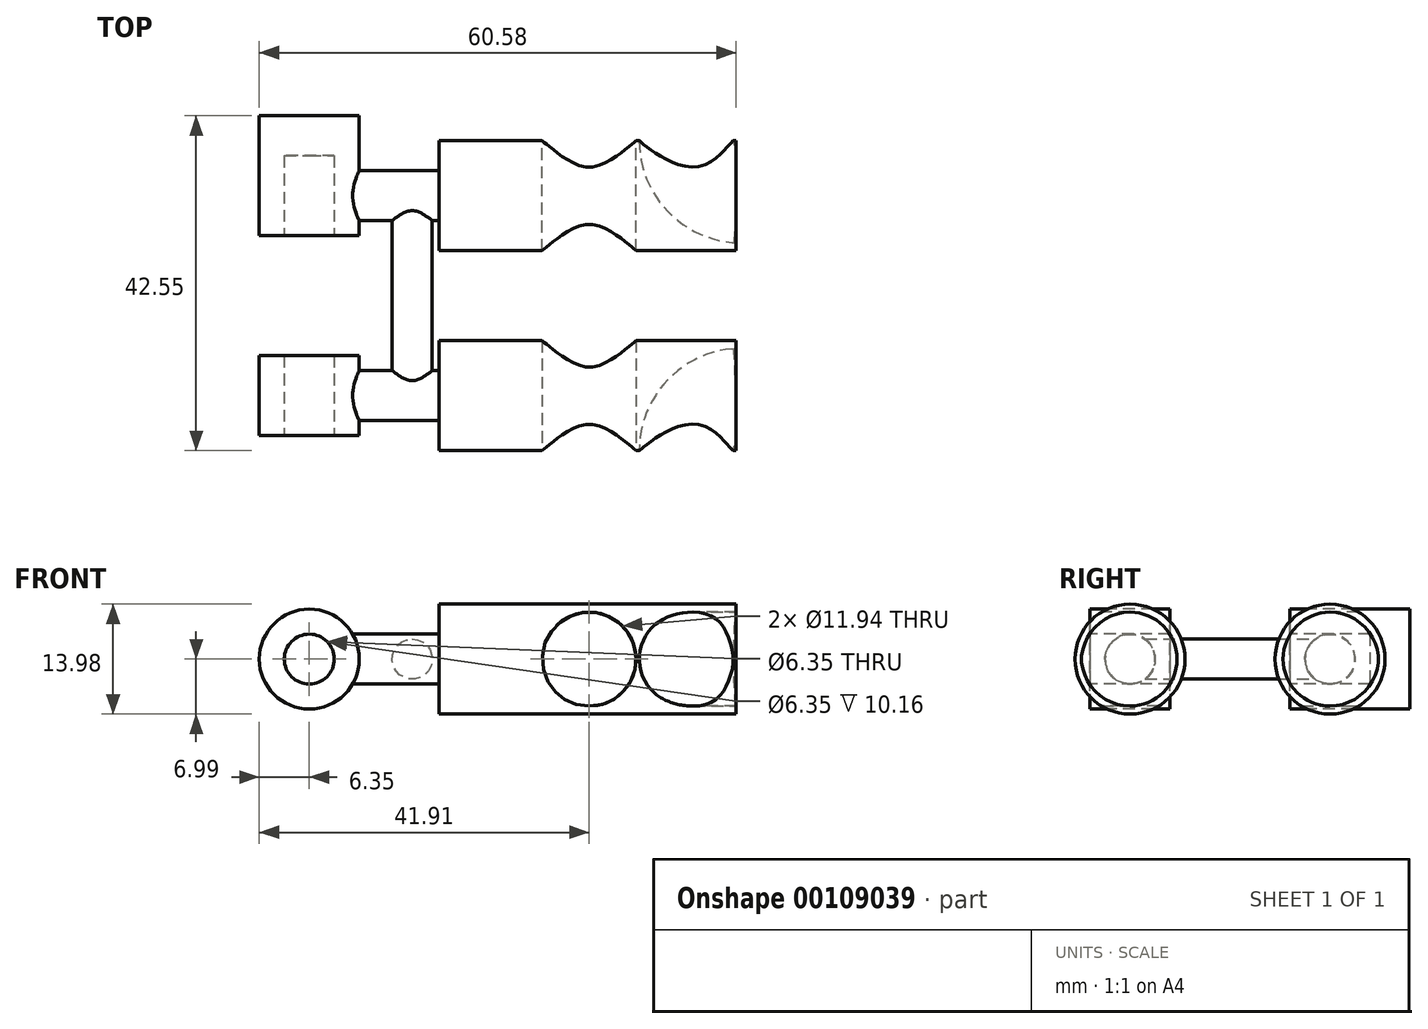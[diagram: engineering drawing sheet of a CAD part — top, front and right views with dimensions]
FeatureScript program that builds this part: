
annotation { "Feature Type Name" : "Feature", "Feature Type Description" : "" }
export const myFeature = defineFeature(function(context is Context, id is Id, definition is map)
    precondition{}
    {
        {
            var Q0;
            Q0=qCreatedBy(makeId("Right.planeOp"),FACE);
            var sketch = newSketch(context, id + "F0", { "sketchPlane" : qUnion([Q0])});
            skCircle(sketch, "E0", {"center": v(0, 0) * mm, "radius": 6.99 * mm});
            skSolve(sketch);
        }
        {
            var Q0;
            Q0=makeQuery(id+"F0.imprint","IMPRINT",FACE,{"disambiguationData":[TD([[makeQuery(id+"F0.imprint","IMPRINT",EDGE,{"derivedFrom":sQuery(id+"F0.wireOp",EDGE,"E0")}),1.0]])]});
            extrude(context, id + "F1", {"entities" : qUnion([Q0]), "depth" : 35.56 * mm, "hasSecondDirection" : true, "secondDirectionOppositeDirection" : true, "secondDirectionDepth" : 12.7 * mm});
        }
        {
            var Q0;
            Q0=qCreatedBy(makeId("Top.planeOp"),FACE);
            var sketch = newSketch(context, id + "F2", { "sketchPlane" : qUnion([Q0])});
            skLineSegment(sketch, "E1", {"start": v(35.56, 0) * mm, "end": v(29.46, 0) * mm});
            skSolve(sketch);
        }
        {
            var Q0;
            Q0=qCreatedBy(makeId("Top.planeOp"),FACE);
            var sketch = newSketch(context, id + "F3", { "sketchPlane" : qUnion([Q0])});
            skLineSegment(sketch, "E2", {"start": v(6.35, 0) * mm, "end": v(6.35, 17.43) * mm});
            skLineSegment(sketch, "E3", {"start": v(6.35, 0) * mm, "end": v(6.35, -16.9) * mm});
            skLineSegment(sketch, "E4", {"start": v(0, 0) * mm, "end": v(6.35, 0) * mm});
            skLineSegment(sketch, "E5", {"start": v(0, 0) * mm, "end": v(29.46, 0) * mm});
            skSolve(sketch);
        }
        {
            var Q0;
            Q0=qCreatedBy(makeId("Front.planeOp"),FACE);
            var sketch = newSketch(context, id + "F4", { "sketchPlane" : qUnion([Q0])});
            skCircle(sketch, "E6", {"center": v(6.35, 0) * mm, "radius": 5.97 * mm});
            skSolve(sketch);
        }
        {
            var Q0;
            Q0=makeQuery(id+"F4.imprint","IMPRINT",FACE,{"disambiguationData":[TD([[makeQuery(id+"F4.imprint","IMPRINT",EDGE,{"derivedFrom":sQuery(id+"F4.wireOp",EDGE,"E6")}),1.0]])]});
            extrude(context, id + "F5", {"entities" : qUnion([Q0]), "operationType" : NewBodyOperationType.REMOVE, "oppositeDirection" : true, "depth" : 25.4 * mm, "hasSecondDirection" : true, "secondDirectionOppositeDirection" : false, "secondDirectionDepth" : 25.4 * mm});
        }
        {
            var Q0;
            Q0=qCreatedBy(makeId("Front.planeOp"),FACE);
            var sketch = newSketch(context, id + "F6", { "sketchPlane" : qUnion([Q0])});
            skLineSegment(sketch, "E7", {"start": v(6.35, 0) * mm, "end": v(18.67, 0) * mm});
            skSolve(sketch);
        }
        {
            var Q0;
            Q0=qCreatedBy(makeId("Front.planeOp"),FACE);
            cPlane(context, id + "F7", {"entities" : qUnion([Q0]), "cplaneType" : CPlaneType.OFFSET, "offset" : 25.4 * mm, "width" : 152.4 * mm, "height" : 152.4 * mm});
        }
        {
            var Q0;
            Q0=qCreatedBy(id+"F7.planeOp",FACE);
            var sketch = newSketch(context, id + "F8", { "sketchPlane" : qUnion([Q0])});
            skCircle(sketch, "E8", {"center": v(18.67, 0) * mm, "radius": 5.97 * mm});
            skLineSegment(sketch, "E9", {"start": v(24.64, 0) * mm, "end": v(25.02, 0) * mm});
            skLineSegment(sketch, "E10", {"start": v(25.02, 0) * mm, "end": v(35.56, 0) * mm});
            skLineSegment(sketch, "E11", {"start": v(12.32, 0) * mm, "end": v(12.7, 0) * mm});
            skSolve(sketch);
        }
        {
            var Q0;
            Q0=makeQuery(id+"F1.opExtrude","CAP_FACE",FACE,{"disambiguationData":[OSD([sQuery(id+"F0.wireOp",EDGE,"E0")])],"isStart":false});
            var Q1;
            Q1=sQuery(id+"F8.wireOp",EDGE,"E10");
            sweep(context, id + "F9", {"operationType" : NewBodyOperationType.REMOVE, "profiles" : qUnion([Q0]), "path" : qUnion([Q1])});
        }
        {
            var Q0;
            Q0=qCreatedBy(makeId("Front.planeOp"),FACE);
            cPlane(context, id + "F10", {"entities" : qUnion([Q0]), "cplaneType" : CPlaneType.OFFSET, "offset" : 12.7 * mm, "oppositeDirection" : true, "width" : 152.4 * mm, "height" : 152.4 * mm});
        }
        {
            var Q0;
            Q0=qCreatedBy(makeId("Top.planeOp"),FACE);
            var sketch = newSketch(context, id + "F11", { "sketchPlane" : qUnion([Q0])});
            skLineSegment(sketch, "E12", {"start": v(25.02, 0) * mm, "end": v(34.29, 0) * mm});
            skLineSegment(sketch, "E13", {"start": v(25.02, 0) * mm, "end": v(25.02, 25.4) * mm});
            skArc(sketch, "E14", {"start": v(34.29, 0) * mm, "mid": v(38.78, 1.86) * mm, "end": v(40.64, 6.35) * mm});
            skLineSegment(sketch, "E15", {"start": v(40.64, 6.35) * mm, "end": v(40.64, 19.05) * mm});
            skArc(sketch, "E16", {"start": v(40.64, 19.05) * mm, "mid": v(38.78, 23.54) * mm, "end": v(34.29, 25.4) * mm});
            skLineSegment(sketch, "E17", {"start": v(25.02, 25.4) * mm, "end": v(34.29, 25.4) * mm});
            skLineSegment(sketch, "E18", {"start": v(-29.21, 25.4) * mm, "end": v(-12.7, 25.4) * mm});
            skLineSegment(sketch, "E19", {"start": v(-29.21, 0) * mm, "end": v(-12.7, 0) * mm});
            skLineSegment(sketch, "E20", {"start": v(-12.7, 0) * mm, "end": v(-12.7, 25.4) * mm});
            skSolve(sketch);
        }
        {
            var Q0;
            Q0=makeQuery(id+"F9.boolean.opBoolean","COPY",FACE,{"derivedFrom":makeQuery(id+"F9.opSweep","CAP_FACE",FACE,{"disambiguationData":[OSD([sQuery(id+"F0.wireOp",EDGE,"E0"),sQuery(id+"F8.wireOp",VERTEX,"E10.start")])],"isStart":false})});
            var sketch = newSketch(context, id + "F12", { "sketchPlane" : qUnion([Q0])});
            skCircle(sketch, "E21", {"center": v(0, 0) * mm, "radius": 3.18 * mm});
            skSolve(sketch);
        }
        {
            var Q0;
            Q0=makeQuery(id+"F1.opExtrude","CAP_FACE",FACE,{"disambiguationData":[OSD([sQuery(id+"F0.wireOp",EDGE,"E0")])],"isStart":true});
            var sketch = newSketch(context, id + "F13", { "sketchPlane" : qUnion([Q0])});
            skCircle(sketch, "E22", {"center": v(0, 0) * mm, "radius": 3.18 * mm});
            skSolve(sketch);
        }
        {
            var Q0;
            Q0=qCreatedBy(makeId("Top.planeOp"),FACE);
            var sketch = newSketch(context, id + "F14", { "sketchPlane" : qUnion([Q0])});
            skLineSegment(sketch, "E23", {"start": v(0, 0) * mm, "end": v(-7.6, 0) * mm});
            skLineSegment(sketch, "E24", {"start": v(18.67, -25.4) * mm, "end": v(18.67, -6.99) * mm});
            skLineSegment(sketch, "E25", {"start": v(18.67, -6.99) * mm, "end": v(18.67, 0) * mm});
            skArc(sketch, "E26", {"start": v(18.67, -6.99) * mm, "mid": v(20.5, -2.27) * mm, "end": v(25.02, 0) * mm});
            skLineSegment(sketch, "E27", {"start": v(25.02, 0) * mm, "end": v(37.77, 0) * mm});
            skSolve(sketch);
        }
        {
            var Q0;
            {var subQ0=sQuery(id+"F8.wireOp",EDGE,"E8");var subQ1=makeQuery(id+"F8.imprint","IMPRINT",VERTEX,{"disambiguationData":[OD(0.0)],"derivedFrom":subQ0});Q0=makeQuery(id+"F8.imprint","IMPRINT",FACE,{"disambiguationData":[TD([[makeQuery(id+"F8.imprint","IMPRINT",EDGE,{"disambiguationData":[TD([[subQ1,-1.0]])],"derivedFrom":subQ0}),1.0]])]});}
            var Q1;
            Q1=sQuery(id+"F14.wireOp",EDGE,"E24");
            var Q2;
            Q2=sQuery(id+"F14.wireOp",EDGE,"E26");
            var Q3;
            Q3=sQuery(id+"F14.wireOp",EDGE,"E27");
            sweep(context, id + "F15", {"operationType" : NewBodyOperationType.REMOVE, "profiles" : qUnion([Q0]), "path" : qUnion([Q1, Q2, Q3])});
        }
        {
            var Q0;
            Q0=makeQuery(id+"F1.opExtrude","SWEPT_BODY",BODY,{"disambiguationData":[OSD([sQuery(id+"F0.wireOp",EDGE,"E0")])]});
            var Q1;
            Q1=qCreatedBy(id+"F10.planeOp",FACE);
            mirror(context, id + "F16", {"entities" : qUnion([Q0]), "mirrorPlane" : qUnion([Q1])});
        }
        {
            var Q0;
            Q0=sQuery(id+"F11.wireOp",EDGE,"E19");
            cPlane(context, id + "F17", {"entities" : qUnion([Q0]), "cplaneType" : CPlaneType.LINE_ANGLE, "offset" : 25.4 * mm, "angle" : 0 * degree, "width" : 152.4 * mm, "height" : 152.4 * mm});
        }
        {
            var Q0;
            Q0=qCreatedBy(id+"F17.planeOp",FACE);
            var sketch = newSketch(context, id + "F18", { "sketchPlane" : qUnion([Q0])});
            skCircle(sketch, "E28", {"center": v(29.21, 0) * mm, "radius": 3.18 * mm});
            skCircle(sketch, "E29", {"center": v(29.21, 0) * mm, "radius": 6.35 * mm});
            skCircle(sketch, "E30", {"center": v(16.14, 0) * mm, "radius": 1.27 * mm});
            skSolve(sketch);
        }
        {
            var Q0;
            Q0=makeQuery(id+"F13.imprint","IMPRINT",FACE,{"disambiguationData":[TD([[makeQuery(id+"F13.imprint","IMPRINT",EDGE,{"derivedFrom":sQuery(id+"F13.wireOp",EDGE,"E22")}),1.0]])]});
            extrude(context, id + "F19", {"entities" : qUnion([Q0]), "operationType" : NewBodyOperationType.ADD, "depth" : 16.5 * mm});
        }
        {
            var Q0;
            Q0=sQuery(id+"F11.wireOp",EDGE,"E18");
            cPlane(context, id + "F20", {"entities" : qUnion([Q0]), "cplaneType" : CPlaneType.LINE_ANGLE, "offset" : 25.4 * mm, "angle" : 0 * degree, "width" : 152.4 * mm, "height" : 152.4 * mm});
        }
        {
            var Q0;
            Q0=qCreatedBy(id+"F20.planeOp",FACE);
            var sketch = newSketch(context, id + "F21", { "sketchPlane" : qUnion([Q0])});
            skCircle(sketch, "E31", {"center": v(16.14, 0) * mm, "radius": 2.54 * mm});
            skCircle(sketch, "E32", {"center": v(29.21, 0) * mm, "radius": 3.18 * mm});
            skCircle(sketch, "E33", {"center": v(29.21, 0) * mm, "radius": 6.35 * mm});
            skSolve(sketch);
        }
        {
            var Q0;
            Q0=makeQuery(id+"F16.opPattern","COPY",FACE,{"derivedFrom":makeQuery(id+"F1.opExtrude","CAP_FACE",FACE,{"disambiguationData":[OSD([sQuery(id+"F0.wireOp",EDGE,"E0")])],"isStart":true}),"instanceName":"1"});
            var sketch = newSketch(context, id + "F22", { "sketchPlane" : qUnion([Q0])});
            skCircle(sketch, "E34", {"center": v(-25.4, 0) * mm, "radius": 3.18 * mm});
            skSolve(sketch);
        }
        {
            var Q0;
            Q0=makeQuery(id+"F22.imprint","IMPRINT",FACE,{"disambiguationData":[TD([[makeQuery(id+"F22.imprint","IMPRINT",EDGE,{"derivedFrom":sQuery(id+"F22.wireOp",EDGE,"E34")}),1.0]])]});
            extrude(context, id + "F23", {"entities" : qUnion([Q0]), "operationType" : NewBodyOperationType.ADD, "depth" : 16.5 * mm});
        }
        {
            var Q0;
            Q0=makeQuery(id+"F21.imprint","IMPRINT",FACE,{"disambiguationData":[TD([[makeQuery(id+"F21.imprint","IMPRINT",EDGE,{"derivedFrom":sQuery(id+"F21.wireOp",EDGE,"E31")}),1.0]])]});
            var Q1;
            Q1=sQuery(id+"F21.wireOp",EDGE,"E31");
            extrude(context, id + "F24", {"entities" : qUnion([Q0]), "operationType" : NewBodyOperationType.ADD, "surfaceEntities" : qUnion([Q1]), "oppositeDirection" : true, "depth" : 25.4 * mm});
        }
        {
            var Q0;
            Q0=makeQuery(id+"F21.imprint","IMPRINT",FACE,{"disambiguationData":[TD([[makeQuery(id+"F21.imprint","IMPRINT",EDGE,{"derivedFrom":sQuery(id+"F21.wireOp",EDGE,"E32")}),1.0]])]});
            extrude(context, id + "F25", {"entities" : qUnion([Q0]), "operationType" : NewBodyOperationType.REMOVE, "depth" : 25.4 * mm, "hasSecondDirection" : true, "secondDirectionOppositeDirection" : true, "secondDirectionDepth" : 32.76 * mm});
        }
        {
            var Q0;
            Q0=makeQuery(id+"F21.imprint","IMPRINT",FACE,{"disambiguationData":[TD([[makeQuery(id+"F21.imprint","IMPRINT",EDGE,{"derivedFrom":sQuery(id+"F21.wireOp",EDGE,"E32")}),-1.0]])]});
            var Q1;
            Q1=makeQuery(id+"F18.imprint","IMPRINT",FACE,{"disambiguationData":[TD([[makeQuery(id+"F18.imprint","IMPRINT",EDGE,{"derivedFrom":sQuery(id+"F18.wireOp",EDGE,"E28")}),-1.0]])]});
            extrude(context, id + "F26", {"entities" : qUnion([Q0, Q1]), "operationType" : NewBodyOperationType.ADD, "depth" : 5.08 * mm, "hasSecondDirection" : true, "secondDirectionOppositeDirection" : true, "secondDirectionDepth" : 5.08 * mm});
        }
        {
            var Q0;
            Q0=makeQuery(id+"F26.opExtrude","CAP_FACE",FACE,{"disambiguationData":[OSD([sQuery(id+"F21.wireOp",EDGE,"E32"),sQuery(id+"F21.wireOp",EDGE,"E33")])],"isStart":false});
            var sketch = newSketch(context, id + "F27", { "sketchPlane" : qUnion([Q0])});
            skCircle(sketch, "E35", {"center": v(29.21, 0) * mm, "radius": 6.35 * mm});
            skSolve(sketch);
        }
        {
            var Q0;
            Q0=makeQuery(id+"F27.imprint","IMPRINT",FACE,{"disambiguationData":[TD([[makeQuery(id+"F27.imprint","IMPRINT",EDGE,{"derivedFrom":sQuery(id+"F27.wireOp",EDGE,"E35")}),1.0]])]});
            var Q1;
            Q1=makeQuery(id+"F27.imprint","IMPRINT",FACE,{"disambiguationData":[TD([[makeQuery(id+"F27.imprint","IMPRINT",EDGE,{"derivedFrom":makeQuery(id+"F26.opExtrude","CAP_EDGE",EDGE,{"disambiguationData":[OSD([sQuery(id+"F21.wireOp",EDGE,"E32")])],"isStart":false})}),1.0]])]});
            extrude(context, id + "F28", {"entities" : qUnion([Q0, Q1]), "operationType" : NewBodyOperationType.ADD, "depth" : 5.08 * mm});
        }
    });
